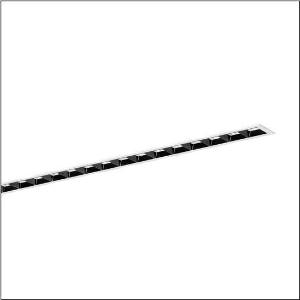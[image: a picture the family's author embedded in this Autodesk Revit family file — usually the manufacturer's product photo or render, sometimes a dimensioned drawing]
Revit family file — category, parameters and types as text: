
# Revit family: silica_r__21_51mx12dc3awb_9b9c
name_source: partatom
category: Lighting Fixtures
units: mm (PartAtom-declared; Revit-internal decimal feet)

## family parameters
Cut with Voids When Loaded = No
Host = Face
Light Source = No
Part Type = Normal
Room Calculation Point = No
Round Connector Dimension = Use Diameter
Shared = No

## types (1)
- --- (1 x LED, 10800 lm, 69.2 W, 3000K)
    Apparent Load = 69 VA
    CIE Flux Codes = 86 100 100 100 100
    Color Rendering = 80
    Color Temperature = 3000K
    Default Elevation = 1800 mm
    Description = Silica® 21, office luminaire, primary light control with darklight reflector, of PMMA, black, CAT 2 (L<= 3000cd/m²), light emission: direct distribution, primary light characteristic: symmetric, installation type: recessed, LED, rated luminous flux: 10.800lm, luminous efficacy: 156lm/W, light colour: 830, colour temperature: 3000K, with terminal, 3+2-pole, max. 2.5mm², mains connection: 220..240V, AC, 50/60Hz, rated input power: 69.2W, luminaire housing, of aluminium, traffic white (RAL 9016), length: 3.028mm, width: 79mm, height: 53mm, protection rating (complete): IP20, insulation class (complete): insulation class I (protective earthing), certification: CE, permissible operating ambient temperature: 0..+35°C, standard: EN 50419, packaging unit: 1 piece
    Height = 0 mm  [stored 0 ft]
    Lamp = 1 x LED
    Lamp Light Flux = 10800 lm
    Lamp Power = 69.2 W
    Lamp count = 1
    Length = 3027 mm
    Luminous efficacy = 156 lm/W
    Manufacturer = Siteco
    ModVariant = No
    Model = 51MX12DC3AWB
    Mounting Place = Ceiling
    Mounting Type = Recessed
    Number of Poles = 1
    OnlyDefault = Yes
    Power Factor = 1
    Product Name = Silica® 21
    Product group = office luminaire | ceiling recessed
    ProductGroupID = 401
    Protection Class = Protection class I
    Protection Degree = IP 20
    RLX_Detail_Level = 1
    RLX_Emergency_Light_Flux = 0 lm
    RLX_Emergency_Type = 0
    RLX_Emergency_Type_DB = No
    RlxData = <blob elided: 63085 chars, md5=e54751e9>
    Socket = socket
    Standby Power = 0 W
    System Light Flux = 10800 lm
    System Power = 69 W
    Type Comments = factory setting: luminous flux: 100 % | dim-lin: 254 | 392 mA
    Type Image = l_1313610.jpg
    URL = http://relux.com
    VarID = @adj_073693
    Voltage = 0 V
    Weight = 0.00 kg
    Width = 79 mm

note: [stored X ft] marks values corroborated as IEEE doubles in the binary element streams (Revit-internal decimal feet)

## geometry (parser evidence)
native form markers: Blend x4, Sweep x10
no freeform markers — native parametric forms only
